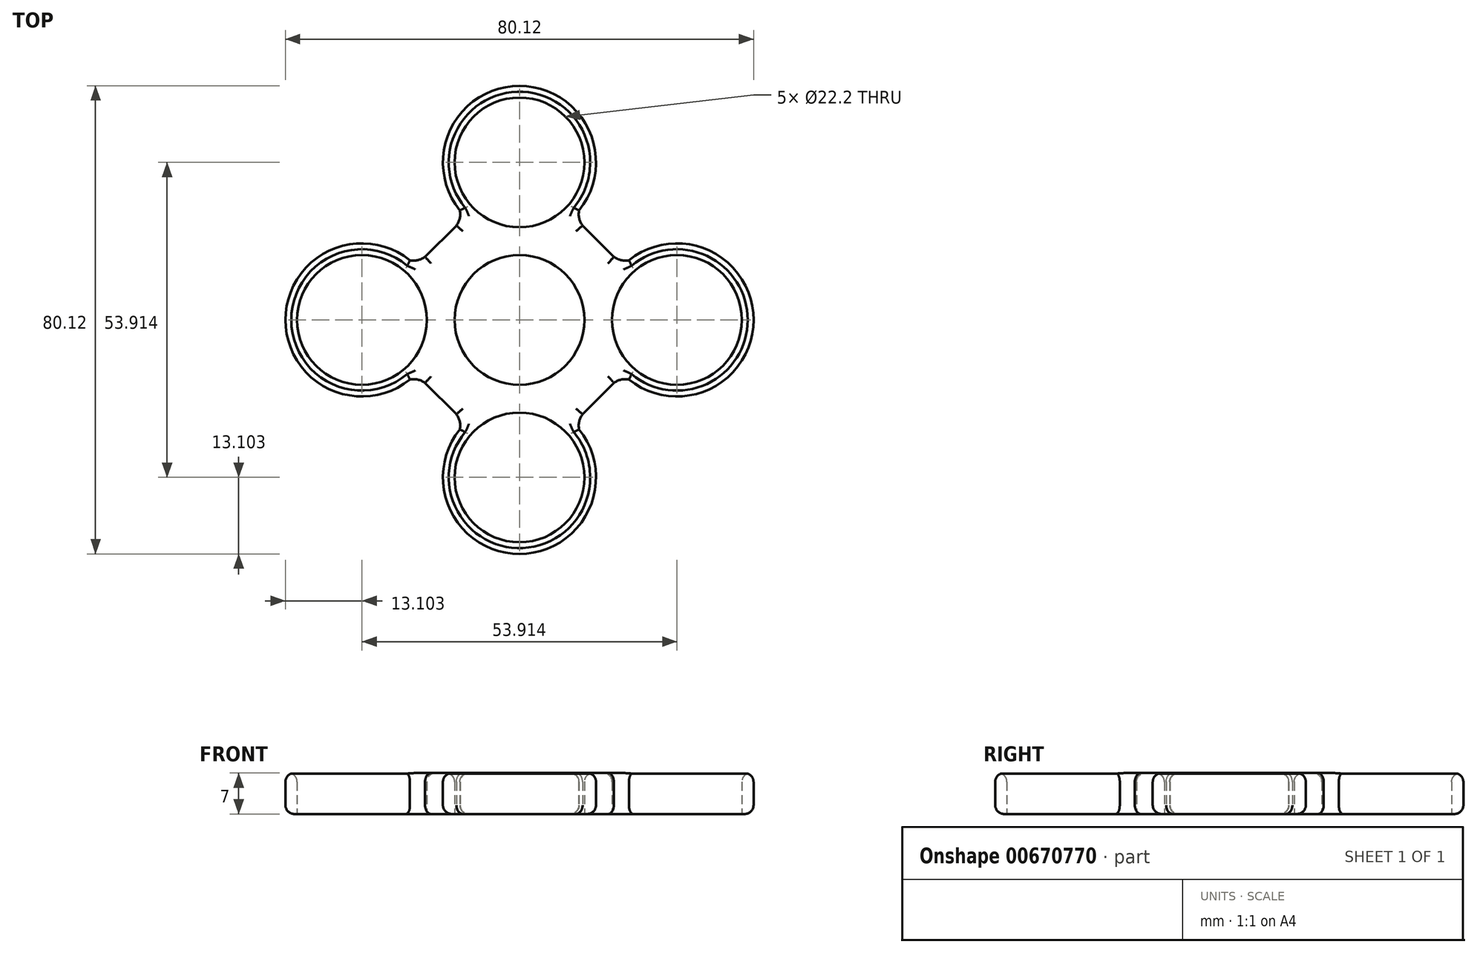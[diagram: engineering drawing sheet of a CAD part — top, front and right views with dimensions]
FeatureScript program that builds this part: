
annotation { "Feature Type Name" : "Feature", "Feature Type Description" : "" }
export const myFeature = defineFeature(function(context is Context, id is Id, definition is map)
    precondition{}
    {
        {
            var Q0;
            Q0=qCreatedBy(makeId("Top.planeOp"),FACE);
            var sketch = newSketch(context, id + "F0", { "sketchPlane" : qUnion([Q0])});
            skCircle(sketch, "E0", {"center": v(0, 0) * mm, "radius": 11.1 * mm});
            skCircle(sketch, "E1", {"center": v(0, 26.96) * mm, "radius": 11.1 * mm});
            skArc(sketch, "E2", {"start": v(10.2, 18.74) * mm, "mid": v(0, 40.06) * mm, "end": v(-10.2, 18.74) * mm});
            skCircle(sketch, "E3.1.0", {"center": v(-26.96, 0) * mm, "radius": 11.1 * mm});
            skArc(sketch, "E3.1.1", {"start": v(-18.74, 10.2) * mm, "mid": v(-40.06, 0) * mm, "end": v(-18.74, -10.2) * mm});
            skCircle(sketch, "E3.2.0", {"center": v(0, -26.96) * mm, "radius": 11.1 * mm});
            skArc(sketch, "E3.2.1", {"start": v(-10.2, -18.74) * mm, "mid": v(0, -40.06) * mm, "end": v(10.2, -18.74) * mm});
            skCircle(sketch, "E3.3.0", {"center": v(26.96, 0) * mm, "radius": 11.1 * mm});
            skArc(sketch, "E3.3.1", {"start": v(18.74, -10.2) * mm, "mid": v(40.06, 0) * mm, "end": v(18.74, 10.2) * mm});
            skLineSegment(sketch, "E4", {"start": v(-16.16, 10.8) * mm, "end": v(-10.8, 16.16) * mm});
            skLineSegment(sketch, "E5.1.0", {"start": v(-10.8, -16.16) * mm, "end": v(-16.16, -10.8) * mm});
            skLineSegment(sketch, "E5.2.0", {"start": v(16.16, -10.8) * mm, "end": v(10.8, -16.16) * mm});
            skLineSegment(sketch, "E5.3.0", {"start": v(10.8, 16.16) * mm, "end": v(16.16, 10.8) * mm});
            skArc(sketch, "E6", {"start": v(-18.74, 10.2) * mm, "mid": v(-17.39, 10.22) * mm, "end": v(-16.16, 10.8) * mm});
            skArc(sketch, "E7.MirrorCS", {"start": v(-10.2, 18.74) * mm, "mid": v(-10.22, 17.39) * mm, "end": v(-10.8, 16.16) * mm});
            skArc(sketch, "E8.1.0", {"start": v(-18.74, -10.2) * mm, "mid": v(-17.39, -10.22) * mm, "end": v(-16.16, -10.8) * mm});
            skArc(sketch, "E8.1.1", {"start": v(-10.2, -18.74) * mm, "mid": v(-10.22, -17.39) * mm, "end": v(-10.8, -16.16) * mm});
            skArc(sketch, "E8.2.0", {"start": v(10.2, -18.74) * mm, "mid": v(10.22, -17.39) * mm, "end": v(10.8, -16.16) * mm});
            skArc(sketch, "E8.2.1", {"start": v(18.74, -10.2) * mm, "mid": v(17.39, -10.22) * mm, "end": v(16.16, -10.8) * mm});
            skArc(sketch, "E8.3.0", {"start": v(18.74, 10.2) * mm, "mid": v(17.39, 10.22) * mm, "end": v(16.16, 10.8) * mm});
            skArc(sketch, "E8.3.1", {"start": v(10.2, 18.74) * mm, "mid": v(10.22, 17.39) * mm, "end": v(10.8, 16.16) * mm});
            skSolve(sketch);
        }
        {
            var Q0;
            Q0 = qSketchRegion(id + "F0", true);
            extrude(context, id + "F1", {"entities" : qUnion([Q0]), "depth" : 7 * mm, "offsetDistance" : 25 * mm});
        }
        {
            var Q0;
            Q0=makeQuery(id+"F1.opExtrude","CAP_EDGE",EDGE,{"disambiguationData":[OSD([sQuery(id+"F0.wireOp",EDGE,"E3.1.1")])],"isStart":false});
            var Q1;
            Q1=makeQuery(id+"F1.opExtrude","CAP_EDGE",EDGE,{"disambiguationData":[OSD([sQuery(id+"F0.wireOp",EDGE,"E4")])],"isStart":false});
            var Q2;
            Q2=makeQuery(id+"F1.opExtrude","CAP_EDGE",EDGE,{"disambiguationData":[OSD([sQuery(id+"F0.wireOp",EDGE,"E5.1.0")])],"isStart":false});
            var Q3;
            Q3=makeQuery(id+"F1.opExtrude","CAP_EDGE",EDGE,{"disambiguationData":[OSD([sQuery(id+"F0.wireOp",EDGE,"E3.2.1")])],"isStart":false});
            var Q4;
            Q4=makeQuery(id+"F1.opExtrude","CAP_EDGE",EDGE,{"disambiguationData":[OSD([sQuery(id+"F0.wireOp",EDGE,"E5.2.0")])],"isStart":false});
            var Q5;
            Q5=makeQuery(id+"F1.opExtrude","CAP_EDGE",EDGE,{"disambiguationData":[OSD([sQuery(id+"F0.wireOp",EDGE,"E3.3.1")])],"isStart":false});
            var Q6;
            Q6=makeQuery(id+"F1.opExtrude","CAP_EDGE",EDGE,{"disambiguationData":[OSD([sQuery(id+"F0.wireOp",EDGE,"E5.3.0")])],"isStart":false});
            var Q7;
            Q7=makeQuery(id+"F1.opExtrude","CAP_EDGE",EDGE,{"disambiguationData":[OSD([sQuery(id+"F0.wireOp",EDGE,"E2")])],"isStart":false});
            var Q8;
            Q8=makeQuery(id+"F1.opExtrude","CAP_EDGE",EDGE,{"disambiguationData":[OSD([sQuery(id+"F0.wireOp",EDGE,"E6")])],"isStart":false});
            var Q9;
            Q9=makeQuery(id+"F1.opExtrude","CAP_EDGE",EDGE,{"disambiguationData":[OSD([sQuery(id+"F0.wireOp",EDGE,"E8.1.0")])],"isStart":false});
            var Q10;
            Q10=makeQuery(id+"F1.opExtrude","CAP_EDGE",EDGE,{"disambiguationData":[OSD([sQuery(id+"F0.wireOp",EDGE,"E7.MirrorCS")])],"isStart":false});
            var Q11;
            Q11=makeQuery(id+"F1.opExtrude","CAP_EDGE",EDGE,{"disambiguationData":[OSD([sQuery(id+"F0.wireOp",EDGE,"E8.3.1")])],"isStart":false});
            var Q12;
            Q12=makeQuery(id+"F1.opExtrude","CAP_EDGE",EDGE,{"disambiguationData":[OSD([sQuery(id+"F0.wireOp",EDGE,"E8.3.0")])],"isStart":false});
            var Q13;
            Q13=makeQuery(id+"F1.opExtrude","CAP_FACE",FACE,{"disambiguationData":[OSD([sQuery(id+"F0.wireOp",EDGE,"E0"),sQuery(id+"F0.wireOp",EDGE,"E1"),sQuery(id+"F0.wireOp",EDGE,"E2"),sQuery(id+"F0.wireOp",EDGE,"E3.1.0"),sQuery(id+"F0.wireOp",EDGE,"E3.1.1"),sQuery(id+"F0.wireOp",EDGE,"E3.2.0"),sQuery(id+"F0.wireOp",EDGE,"E3.2.1"),sQuery(id+"F0.wireOp",EDGE,"E3.3.0"),sQuery(id+"F0.wireOp",EDGE,"E3.3.1"),sQuery(id+"F0.wireOp",EDGE,"E4"),sQuery(id+"F0.wireOp",EDGE,"E5.1.0"),sQuery(id+"F0.wireOp",EDGE,"E5.2.0"),sQuery(id+"F0.wireOp",EDGE,"E5.3.0"),sQuery(id+"F0.wireOp",EDGE,"E6"),sQuery(id+"F0.wireOp",EDGE,"E7.MirrorCS"),sQuery(id+"F0.wireOp",EDGE,"E8.1.0"),sQuery(id+"F0.wireOp",EDGE,"E8.1.1"),sQuery(id+"F0.wireOp",EDGE,"E8.2.0"),sQuery(id+"F0.wireOp",EDGE,"E8.2.1"),sQuery(id+"F0.wireOp",EDGE,"E8.3.0"),sQuery(id+"F0.wireOp",EDGE,"E8.3.1")])],"isStart":false});
            var Q14;
            Q14=makeQuery(id+"F1.opExtrude","CAP_EDGE",EDGE,{"disambiguationData":[OSD([sQuery(id+"F0.wireOp",EDGE,"E8.2.0")])],"isStart":false});
            fillet(context, id + "F2", {"entities" : qUnion([Q0, Q1, Q2, Q3, Q4, Q5, Q6, Q7, Q8, Q9, Q10, Q11, Q12, Q13, Q14]), "radius" : 1.5 * mm, "tangentPropagation" : true, "allowEdgeOverflow" : false});
        }
        {
            var Q0;
            Q0=makeQuery(id+"F1.opExtrude","CAP_EDGE",EDGE,{"disambiguationData":[OSD([sQuery(id+"F0.wireOp",EDGE,"E5.3.0")])],"isStart":true});
            var Q1;
            Q1=makeQuery(id+"F1.opExtrude","CAP_EDGE",EDGE,{"disambiguationData":[OSD([sQuery(id+"F0.wireOp",EDGE,"E8.3.1")])],"isStart":true});
            var Q2;
            Q2=makeQuery(id+"F1.opExtrude","CAP_EDGE",EDGE,{"disambiguationData":[OSD([sQuery(id+"F0.wireOp",EDGE,"E8.3.0")])],"isStart":true});
            var Q3;
            Q3=makeQuery(id+"F1.opExtrude","CAP_EDGE",EDGE,{"disambiguationData":[OSD([sQuery(id+"F0.wireOp",EDGE,"E3.3.1")])],"isStart":true});
            var Q4;
            Q4=makeQuery(id+"F1.opExtrude","CAP_EDGE",EDGE,{"disambiguationData":[OSD([sQuery(id+"F0.wireOp",EDGE,"E2")])],"isStart":true});
            var Q5;
            Q5=makeQuery(id+"F1.opExtrude","CAP_EDGE",EDGE,{"disambiguationData":[OSD([sQuery(id+"F0.wireOp",EDGE,"E7.MirrorCS")])],"isStart":true});
            var Q6;
            Q6=makeQuery(id+"F1.opExtrude","CAP_EDGE",EDGE,{"disambiguationData":[OSD([sQuery(id+"F0.wireOp",EDGE,"E4")])],"isStart":true});
            var Q7;
            Q7=makeQuery(id+"F1.opExtrude","CAP_EDGE",EDGE,{"disambiguationData":[OSD([sQuery(id+"F0.wireOp",EDGE,"E6")])],"isStart":true});
            var Q8;
            Q8=makeQuery(id+"F1.opExtrude","CAP_EDGE",EDGE,{"disambiguationData":[OSD([sQuery(id+"F0.wireOp",EDGE,"E3.1.1")])],"isStart":true});
            var Q9;
            Q9=makeQuery(id+"F1.opExtrude","CAP_EDGE",EDGE,{"disambiguationData":[OSD([sQuery(id+"F0.wireOp",EDGE,"E8.1.0")])],"isStart":true});
            var Q10;
            Q10=makeQuery(id+"F1.opExtrude","CAP_EDGE",EDGE,{"disambiguationData":[OSD([sQuery(id+"F0.wireOp",EDGE,"E5.1.0")])],"isStart":true});
            var Q11;
            Q11=makeQuery(id+"F1.opExtrude","CAP_EDGE",EDGE,{"disambiguationData":[OSD([sQuery(id+"F0.wireOp",EDGE,"E8.1.1")])],"isStart":true});
            var Q12;
            Q12=makeQuery(id+"F1.opExtrude","CAP_EDGE",EDGE,{"disambiguationData":[OSD([sQuery(id+"F0.wireOp",EDGE,"E3.2.1")])],"isStart":true});
            var Q13;
            Q13=makeQuery(id+"F1.opExtrude","CAP_EDGE",EDGE,{"disambiguationData":[OSD([sQuery(id+"F0.wireOp",EDGE,"E8.2.0")])],"isStart":true});
            var Q14;
            Q14=makeQuery(id+"F1.opExtrude","CAP_EDGE",EDGE,{"disambiguationData":[OSD([sQuery(id+"F0.wireOp",EDGE,"E5.2.0")])],"isStart":true});
            var Q15;
            Q15=makeQuery(id+"F1.opExtrude","CAP_EDGE",EDGE,{"disambiguationData":[OSD([sQuery(id+"F0.wireOp",EDGE,"E8.2.1")])],"isStart":true});
            fillet(context, id + "F3", {"entities" : qUnion([Q0, Q1, Q2, Q3, Q4, Q5, Q6, Q7, Q8, Q9, Q10, Q11, Q12, Q13, Q14, Q15]), "radius" : 1.5 * mm, "allowEdgeOverflow" : false});
        }
    });
